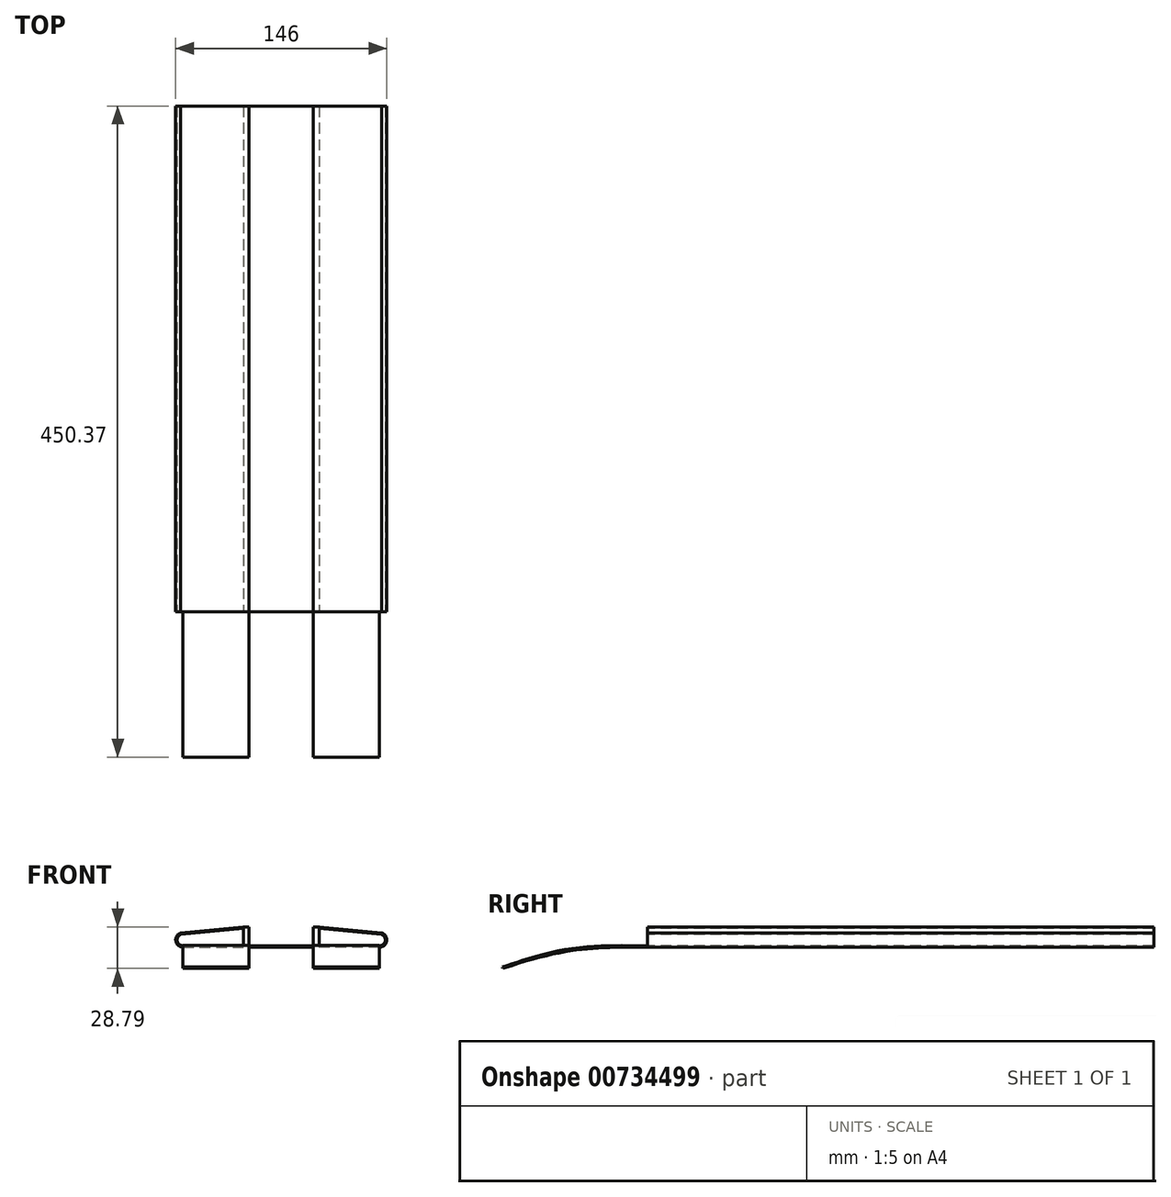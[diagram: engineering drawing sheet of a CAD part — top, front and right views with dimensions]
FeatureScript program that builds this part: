
annotation { "Feature Type Name" : "Feature", "Feature Type Description" : "" }
export const myFeature = defineFeature(function(context is Context, id is Id, definition is map)
    precondition{}
    {
        {
            var Q0;
            Q0=qCreatedBy(makeId("Front.planeOp"),FACE);
            var sketch = newSketch(context, id + "F0", { "sketchPlane" : qUnion([Q0])});
            skLineSegment(sketch, "E0.bottom", {"start": v(-68, 0) * mm, "end": v(0, 0) * mm});
            skLineSegment(sketch, "E1.top", {"start": v(-26.15, 14) * mm, "end": v(-22.25, 14) * mm});
            skLineSegment(sketch, "E1.left", {"start": v(-26.25, 1) * mm, "end": v(-26.25, 13) * mm});
            skLineSegment(sketch, "E1.right", {"start": v(-22.25, 1) * mm, "end": v(-22.25, 14) * mm});
            skLineSegment(sketch, "E2.trimOffspring", {"start": v(-22.25, 1) * mm, "end": v(0, 1) * mm});
            skLineSegment(sketch, "E3", {"start": v(-26.35, 14) * mm, "end": v(-69.47, 9.78) * mm});
            skLineSegment(sketch, "E4", {"start": v(-26.25, 13) * mm, "end": v(-69.27, 8.8) * mm});
            skArc(sketch, "E5", {"start": v(-69.47, 9.78) * mm, "mid": v(-72.94, 4.26) * mm, "end": v(-68, 0) * mm});
            skArc(sketch, "E6.0", {"start": v(-69.27, 8.8) * mm, "mid": v(-71.95, 4.36) * mm, "end": v(-68, 1) * mm});
            skLineSegment(sketch, "E7", {"start": v(-68, 1) * mm, "end": v(-26.25, 1) * mm});
            skPoint(sketch, "E8.visualSharp", {"position": v(-26.25, 14) * mm});
            skArc(sketch, "E8.filletArc", {"start": v(-26.15, 14) * mm, "mid": v(-26.25, 14) * mm, "end": v(-26.35, 14) * mm});
            skArc(sketch, "E9.MirrorCS", {"start": v(-26.02, 14) * mm, "mid": v(-26.25, 13.99) * mm, "end": v(-26.48, 13.95) * mm});
            skLineSegment(sketch, "E10.MirrorCS", {"start": v(-26.02, 14) * mm, "end": v(-22.25, 14) * mm});
            skLineSegment(sketch, "E11.MirrorCS", {"start": v(-26.25, 1) * mm, "end": v(-26.25, 12.97) * mm});
            skArc(sketch, "E12.MirrorCS", {"start": v(26.15, 14) * mm, "mid": v(26.25, 14) * mm, "end": v(26.35, 14) * mm});
            skArc(sketch, "E13.MirrorCS", {"start": v(26.02, 14) * mm, "mid": v(26.25, 13.99) * mm, "end": v(26.48, 13.95) * mm});
            skLineSegment(sketch, "E14.MirrorCS", {"start": v(26.15, 14) * mm, "end": v(22.25, 14) * mm});
            skLineSegment(sketch, "E15.MirrorCS", {"start": v(26.02, 14) * mm, "end": v(22.25, 14) * mm});
            skLineSegment(sketch, "E16.MirrorCS", {"start": v(22.25, 1) * mm, "end": v(22.25, 14) * mm});
            skLineSegment(sketch, "E17.MirrorCS", {"start": v(26.25, 1) * mm, "end": v(26.25, 13) * mm});
            skLineSegment(sketch, "E18.MirrorCS", {"start": v(22.25, 1) * mm, "end": v(0, 1) * mm});
            skLineSegment(sketch, "E19.MirrorCS", {"start": v(68, 0) * mm, "end": v(0, 0) * mm});
            skLineSegment(sketch, "E20.MirrorCS", {"start": v(68, 1) * mm, "end": v(26.25, 1) * mm});
            skPoint(sketch, "E21.MirrorP", {"position": v(26.25, 14) * mm});
            skArc(sketch, "E22.MirrorCS", {"start": v(69.27, 8.8) * mm, "mid": v(71.95, 4.36) * mm, "end": v(68, 1) * mm});
            skArc(sketch, "E23.MirrorCS", {"start": v(69.47, 9.78) * mm, "mid": v(72.94, 4.26) * mm, "end": v(68, 0) * mm});
            skLineSegment(sketch, "E24.MirrorCS", {"start": v(26.25, 13) * mm, "end": v(69.27, 8.8) * mm});
            skLineSegment(sketch, "E25.MirrorCS", {"start": v(26.35, 14) * mm, "end": v(69.47, 9.78) * mm});
            skLineSegment(sketch, "E26.MirrorCS", {"start": v(26.25, 1) * mm, "end": v(26.25, 12.97) * mm});
            skSolve(sketch);
        }
        {
            var Q0;
            Q0=makeQuery(id+"F0.imprint","IMPRINT",FACE,{"disambiguationData":[TD([[makeQuery(id+"F0.imprint","IMPRINT",EDGE,{"derivedFrom":sQuery(id+"F0.wireOp",EDGE,"E1.top")}),-1.0]])]});
            extrude(context, id + "F1", {"entities" : qUnion([Q0]), "oppositeDirection" : true, "depth" : 350 * mm, "offsetDistance" : 25 * mm});
        }
        {
            var Q0;
            Q0=qCreatedBy(makeId("Right.planeOp"),FACE);
            cPlane(context, id + "F2", {"entities" : qUnion([Q0]), "cplaneType" : CPlaneType.OFFSET, "offset" : 22.25 * mm, "oppositeDirection" : true, "width" : 150 * mm, "height" : 150 * mm});
        }
        {
            var Q0;
            Q0=qCreatedBy(id+"F2.planeOp",FACE);
            var sketch = newSketch(context, id + "F3", { "sketchPlane" : qUnion([Q0])});
            skLineSegment(sketch, "E27", {"start": v(0, 0) * mm, "end": v(-100, 0) * mm, "construction": true});
            skFitSpline(sketch, "E28", {"points": [v(0, 0) * mm, v(-100.05, -14.79) * mm], "startDerivative": vector(-110.92, 0) * mm, "endDerivative": vector(-131.3, -44.36) * mm});
            skPoint(sketch, "E29", {"position": v(-50, 0) * mm});
            skFitSpline(sketch, "E30.0", {"points": [v(0, 1) * mm, v(-9.24, 1) * mm, v(-25.54, 1) * mm, v(-47.38, -0.4) * mm, v(-70.52, -4.57) * mm, v(-89.4, -10.14) * mm, v(-100.37, -13.84) * mm]});
            skLineSegment(sketch, "E31", {"start": v(0, 0) * mm, "end": v(0, 1) * mm});
            skLineSegment(sketch, "E32", {"start": v(-100.05, -14.79) * mm, "end": v(-100.37, -13.84) * mm});
            skSolve(sketch);
        }
        {
            var Q0;
            Q0=makeQuery(id+"F3.imprint","IMPRINT",FACE,{"disambiguationData":[TD([[makeQuery(id+"F3.imprint","IMPRINT",EDGE,{"derivedFrom":sQuery(id+"F3.wireOp",EDGE,"E28")}),-1.0]])]});
            extrude(context, id + "F4", {"entities" : qUnion([Q0]), "operationType" : NewBodyOperationType.ADD, "oppositeDirection" : true, "depth" : 45.75 * mm, "offsetDistance" : 25 * mm});
        }
        {
            var Q0;
            Q0=makeQuery(id+"F1.opExtrude","SWEPT_BODY",BODY,{"disambiguationData":[OSD([sQuery(id+"F0.wireOp",EDGE,"E1.top"),sQuery(id+"F0.wireOp",EDGE,"E1.left"),sQuery(id+"F0.wireOp",EDGE,"E3"),sQuery(id+"F0.wireOp",EDGE,"E4"),sQuery(id+"F0.wireOp",EDGE,"E5"),sQuery(id+"F0.wireOp",EDGE,"E6.0"),sQuery(id+"F0.wireOp",EDGE,"E8.filletArc"),sQuery(id+"F0.wireOp",EDGE,"E10.MirrorCS"),sQuery(id+"F0.wireOp",EDGE,"E1.right"),sQuery(id+"F0.wireOp",EDGE,"E0.bottom"),sQuery(id+"F0.wireOp",EDGE,"E2.trimOffspring"),sQuery(id+"F0.wireOp",EDGE,"E11.MirrorCS"),sQuery(id+"F0.wireOp",EDGE,"E7"),sQuery(id+"F0.wireOp",EDGE,"E12.MirrorCS"),sQuery(id+"F0.wireOp",EDGE,"E14.MirrorCS"),sQuery(id+"F0.wireOp",EDGE,"E15.MirrorCS"),sQuery(id+"F0.wireOp",EDGE,"E17.MirrorCS"),sQuery(id+"F0.wireOp",EDGE,"E20.MirrorCS"),sQuery(id+"F0.wireOp",EDGE,"E22.MirrorCS"),sQuery(id+"F0.wireOp",EDGE,"E23.MirrorCS"),sQuery(id+"F0.wireOp",EDGE,"E24.MirrorCS"),sQuery(id+"F0.wireOp",EDGE,"E25.MirrorCS"),sQuery(id+"F0.wireOp",EDGE,"E16.MirrorCS"),sQuery(id+"F0.wireOp",EDGE,"E18.MirrorCS"),sQuery(id+"F0.wireOp",EDGE,"E26.MirrorCS"),sQuery(id+"F0.wireOp",EDGE,"E19.MirrorCS")])]});
            var Q1;
            Q1=qCreatedBy(makeId("Right.planeOp"),FACE);
            mirror(context, id + "F5", {"operationType" : NewBodyOperationType.ADD, "entities" : qUnion([Q0]), "mirrorPlane" : qUnion([Q1])});
        }
    });
